# Revit family: CM216621CocinaPraga180Derecha
name_source: partatom
category: Specialty Equipment
units: mm (PartAtom-declared; Revit-internal decimal feet)

## family parameters
Always vertical = Yes
Cut with Voids When Loaded = No
Part Type = Normal
Room Calculation Point = No
Round Connector Dimension = Use Diameter
Shared = No
Work Plane-Based = No

## types (1)
- CM216621CocinaPraga180Derecha
    Carga Máxima Mueble Inferior = 80 kg
    Carga Máxima Mueble Superior = 38 kg
    Creado por = IDD
    Description = Cocina lista para armar, muy práctica, cómoda y funcional. Se destaca su diseño contemporáneo con una combinación de colores Plomo en su estructura y Gales en sus frentes, generando un contraste de acuerdo a las últimas tendencias en decoración, sus manijas y patas negras, dan un toque único que complementa el diseño de la Cocina. Sus nichos brindan espacios decorativos y de almacenamiento tan útiles en las cocinas abiertas que invitan a tenerlas integradas con el área social.
    Fecha de Creación = 09/10/2020
    Garantía = 1 año en madera y herrajes
    Manufacturer = Corona
    Material Aglomerado = Corona_Madera_Aglomerada_Habano
    Material Alacenas = Corona_Madera_Aglomerada Gris
    Material Patas = Corona_Acero_Negro Mate
    Peso Neto Aprox Módulo Inferior = 42,9 kg
    Peso Neto Aprox Módulo Superior = 50,9 kg
    Referencia = CM0216621
    Resistencia = Mueble resistente al rayado y la abrasión
    Resistencia a la Humedad = hinchamiento < o =8%
    URL = https://corona.co

## geometry (parser evidence)
native form markers: Sweep x22
no freeform markers — native parametric forms only
